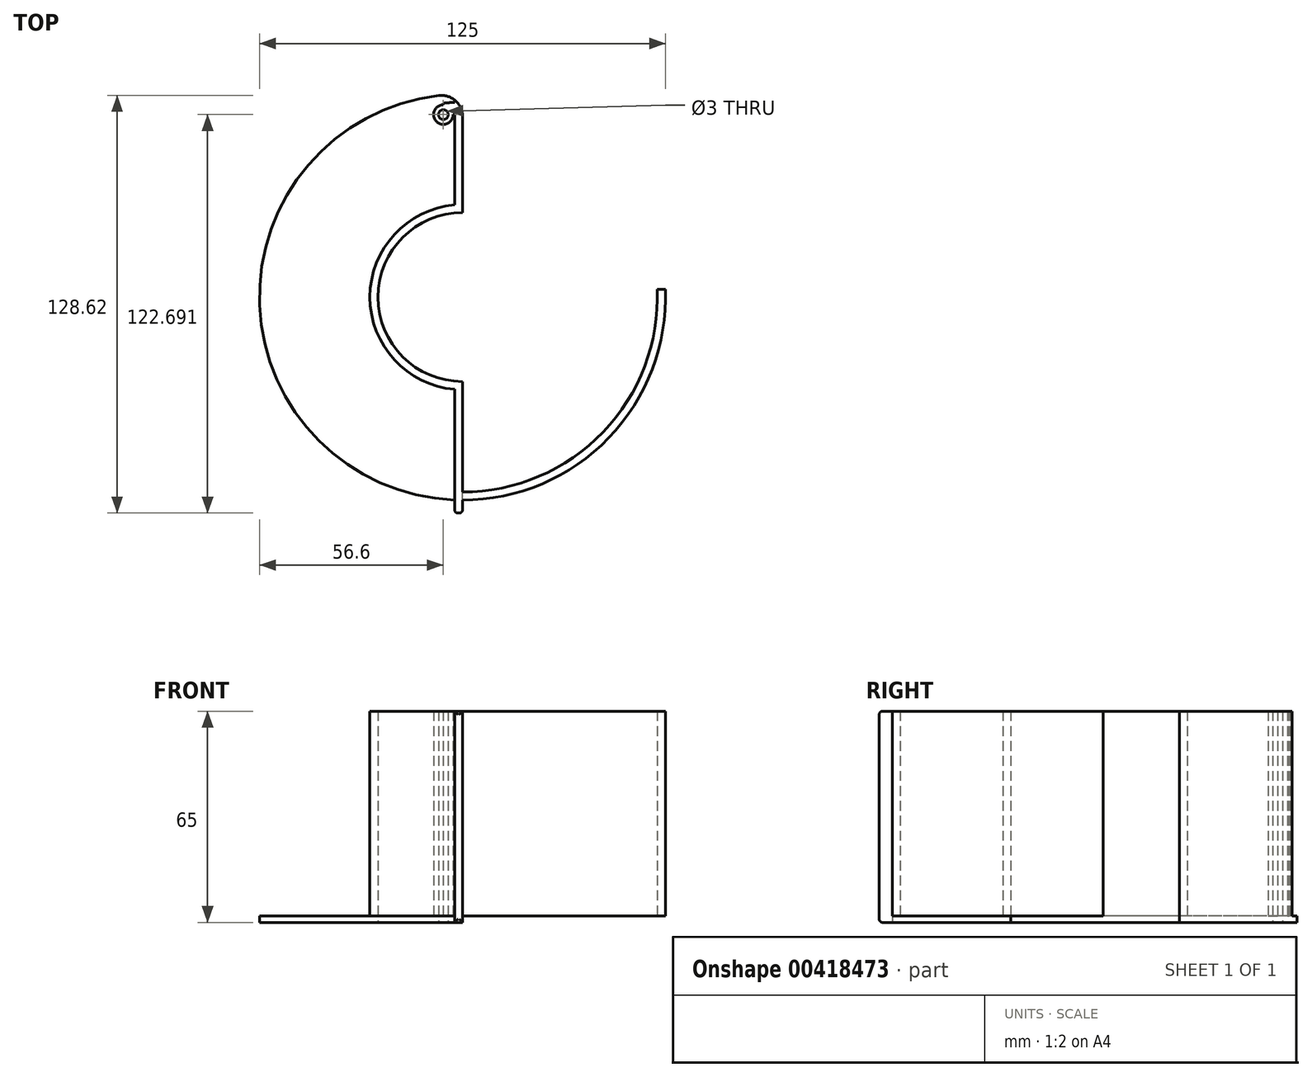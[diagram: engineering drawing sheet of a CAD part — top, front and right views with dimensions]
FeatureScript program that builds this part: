
annotation { "Feature Type Name" : "Feature", "Feature Type Description" : "" }
export const myFeature = defineFeature(function(context is Context, id is Id, definition is map)
    precondition{}
    {
        {
            var Q0;
            Q0=qCreatedBy(makeId("Top.planeOp"),FACE);
            var sketch = newSketch(context, id + "F0", { "sketchPlane" : qUnion([Q0])});
            skCircle(sketch, "E0", {"center": v(0, 0) * mm, "radius": 62.5 * mm});
            skCircle(sketch, "E1", {"center": v(0, 0) * mm, "radius": 26 * mm});
            skCircle(sketch, "E2", {"center": v(0, 0) * mm, "radius": 60 * mm});
            skCircle(sketch, "E3", {"center": v(0, 0) * mm, "radius": 28.5 * mm});
            skLineSegment(sketch, "E4", {"start": v(0, 62.5) * mm, "end": v(0, -62.5) * mm});
            skLineSegment(sketch, "E5", {"start": v(-62.5, 0) * mm, "end": v(62.5, 0) * mm});
            skLineSegment(sketch, "E6", {"start": v(-62.45, 2.4) * mm, "end": v(62.45, 2.4) * mm});
            skLineSegment(sketch, "E7", {"start": v(-2.4, 62.45) * mm, "end": v(-2.4, -62.45) * mm});
            skPoint(sketch, "E8", {"position": v(-5.9, 56.2) * mm});
            skCircle(sketch, "E9", {"center": v(-5.9, 56.2) * mm, "radius": 3 * mm});
            skCircle(sketch, "E10", {"center": v(-5.9, 56.2) * mm, "radius": 1.5 * mm});
            skLineSegment(sketch, "E11", {"start": v(-5.9, 56.2) * mm, "end": v(-5.9, 59.7) * mm});
            skLineSegment(sketch, "E12", {"start": v(-5.9, 56.2) * mm, "end": v(-2.4, 56.2) * mm});
            skPoint(sketch, "E13.orphan", {"position": v(-2.4, 0) * mm});
            skSolve(sketch);
        }
        {
            var Q0;
            Q0=qCreatedBy(makeId("Top.planeOp"),FACE);
            var sketch = newSketch(context, id + "F1", { "sketchPlane" : qUnion([Q0])});
            skCircle(sketch, "E14", {"center": v(0, 0) * mm, "radius": 62.5 * mm});
            skLineSegment(sketch, "E15", {"start": v(0, -62.5) * mm, "end": v(0, 62.5) * mm});
            skLineSegment(sketch, "E16", {"start": v(-62.5, 0) * mm, "end": v(62.5, 0) * mm});
            skCircle(sketch, "E17", {"center": v(0, 0) * mm, "radius": 26 * mm});
            skSolve(sketch);
        }
        {
            var Q0;
            {var subQ0=sQuery(id+"F0.wireOp",EDGE,"E6");var subQ1=sQuery(id+"F0.wireOp",EDGE,"E0");var subQ2=makeQuery(id+"F0.imprint","INTERSECT",VERTEX,{"disambiguationData":[OD(0.0)],"derivedFrom":[subQ1,subQ0]});Q0=makeQuery(id+"F0.imprint","IMPRINT",FACE,{"disambiguationData":[TD([[makeQuery(id+"F0.imprint","IMPRINT",EDGE,{"disambiguationData":[TD([[subQ2,1.0]])],"derivedFrom":subQ1}),1.0]])]});}
            var Q1;
            {var subQ0=sQuery(id+"F0.wireOp",EDGE,"E4");var subQ1=sQuery(id+"F0.wireOp",EDGE,"E0");var subQ2=makeQuery(id+"F0.imprint","INTERSECT",VERTEX,{"disambiguationData":[OD(0.0)],"derivedFrom":[subQ1,subQ0]});Q1=makeQuery(id+"F0.imprint","IMPRINT",FACE,{"disambiguationData":[TD([[makeQuery(id+"F0.imprint","IMPRINT",EDGE,{"disambiguationData":[TD([[subQ2,-1.0]])],"derivedFrom":subQ1}),1.0]])]});}
            var Q2;
            {var subQ0=sQuery(id+"F0.wireOp",EDGE,"E4");var subQ1=sQuery(id+"F0.wireOp",EDGE,"E2");var subQ2=makeQuery(id+"F0.imprint","INTERSECT",VERTEX,{"disambiguationData":[OD(0.0)],"derivedFrom":[subQ1,subQ0]});Q2=makeQuery(id+"F0.imprint","IMPRINT",FACE,{"disambiguationData":[TD([[makeQuery(id+"F0.imprint","IMPRINT",EDGE,{"disambiguationData":[TD([[subQ2,-1.0]])],"derivedFrom":subQ1}),1.0]])]});}
            var Q3;
            {var subQ0=sQuery(id+"F0.wireOp",EDGE,"E4");var subQ1=sQuery(id+"F0.wireOp",EDGE,"E1");var subQ2=makeQuery(id+"F0.imprint","INTERSECT",VERTEX,{"disambiguationData":[OD(0.0)],"derivedFrom":[subQ1,subQ0]});Q3=makeQuery(id+"F0.imprint","IMPRINT",FACE,{"disambiguationData":[TD([[makeQuery(id+"F0.imprint","IMPRINT",EDGE,{"disambiguationData":[TD([[subQ2,-1.0]])],"derivedFrom":subQ1}),-1.0]])]});}
            var Q4;
            {var subQ0=sQuery(id+"F0.wireOp",EDGE,"E7");var subQ1=sQuery(id+"F0.wireOp",EDGE,"E1");var subQ2=makeQuery(id+"F0.imprint","INTERSECT",VERTEX,{"derivedFrom":[subQ1,subQ0]});Q4=makeQuery(id+"F0.imprint","IMPRINT",FACE,{"disambiguationData":[TD([[makeQuery(id+"F0.imprint","IMPRINT",EDGE,{"disambiguationData":[TD([[subQ2,-1.0]])],"derivedFrom":subQ1}),-1.0]])]});}
            var Q5;
            {var subQ0=sQuery(id+"F0.wireOp",EDGE,"E6");var subQ1=sQuery(id+"F0.wireOp",EDGE,"E1");var subQ2=makeQuery(id+"F0.imprint","INTERSECT",VERTEX,{"disambiguationData":[OD(1.0)],"derivedFrom":[subQ1,subQ0]});Q5=makeQuery(id+"F0.imprint","IMPRINT",FACE,{"disambiguationData":[TD([[makeQuery(id+"F0.imprint","IMPRINT",EDGE,{"disambiguationData":[TD([[subQ2,-1.0]])],"derivedFrom":subQ1}),-1.0]])]});}
            var Q6;
            {var subQ0=sQuery(id+"F0.wireOp",EDGE,"E5");var subQ1=sQuery(id+"F0.wireOp",EDGE,"E0");var subQ2=makeQuery(id+"F0.imprint","INTERSECT",VERTEX,{"disambiguationData":[OD(0.0)],"derivedFrom":[subQ1,subQ0]});Q6=makeQuery(id+"F0.imprint","IMPRINT",FACE,{"disambiguationData":[TD([[makeQuery(id+"F0.imprint","IMPRINT",EDGE,{"disambiguationData":[TD([[subQ2,1.0]])],"derivedFrom":subQ1}),1.0]])]});}
            var Q7;
            Q7=makeQuery(id+"F0.imprint","IMPRINT",FACE,{"disambiguationData":[TD([[makeQuery(id+"F0.imprint","IMPRINT",EDGE,{"derivedFrom":sQuery(id+"F0.wireOp",EDGE,"E9")}),1.0]])]});
            var Q8;
            {var subQ0=sQuery(id+"F0.wireOp",EDGE,"E11");var subQ1=sQuery(id+"F0.wireOp",EDGE,"E2");var subQ2=makeQuery(id+"F0.imprint","INTERSECT",VERTEX,{"derivedFrom":[subQ1,subQ0]});Q8=makeQuery(id+"F0.imprint","IMPRINT",FACE,{"disambiguationData":[TD([[makeQuery(id+"F0.imprint","IMPRINT",EDGE,{"disambiguationData":[TD([[subQ2,1.0]])],"derivedFrom":subQ1}),1.0]])]});}
            var Q9;
            {var subQ0=sQuery(id+"F0.wireOp",EDGE,"E5");var subQ1=sQuery(id+"F0.wireOp",EDGE,"E0");var subQ2=makeQuery(id+"F0.imprint","INTERSECT",VERTEX,{"disambiguationData":[OD(0.0)],"derivedFrom":[subQ1,subQ0]});Q9=makeQuery(id+"F0.imprint","IMPRINT",FACE,{"disambiguationData":[TD([[makeQuery(id+"F0.imprint","IMPRINT",EDGE,{"disambiguationData":[TD([[subQ2,-1.0]])],"derivedFrom":subQ1}),1.0]])]});}
            var Q10;
            {var subQ0=sQuery(id+"F0.wireOp",EDGE,"E5");var subQ1=sQuery(id+"F0.wireOp",EDGE,"E1");var subQ2=makeQuery(id+"F0.imprint","INTERSECT",VERTEX,{"disambiguationData":[OD(1.0)],"derivedFrom":[subQ1,subQ0]});Q10=makeQuery(id+"F0.imprint","IMPRINT",FACE,{"disambiguationData":[TD([[makeQuery(id+"F0.imprint","IMPRINT",EDGE,{"disambiguationData":[TD([[subQ2,-1.0]])],"derivedFrom":subQ1}),-1.0]])]});}
            var Q11;
            {var subQ0=sQuery(id+"F0.wireOp",EDGE,"E7");var subQ1=sQuery(id+"F0.wireOp",EDGE,"E2");var subQ2=makeQuery(id+"F0.imprint","INTERSECT",VERTEX,{"disambiguationData":[OD(1.0)],"derivedFrom":[subQ1,subQ0]});Q11=makeQuery(id+"F0.imprint","IMPRINT",FACE,{"disambiguationData":[TD([[makeQuery(id+"F0.imprint","IMPRINT",EDGE,{"disambiguationData":[TD([[subQ2,-1.0]])],"derivedFrom":subQ1}),1.0]])]});}
            var Q12;
            {var subQ0=sQuery(id+"F0.wireOp",EDGE,"E4");var subQ1=sQuery(id+"F0.wireOp",EDGE,"E0");var subQ2=makeQuery(id+"F0.imprint","INTERSECT",VERTEX,{"disambiguationData":[OD(1.0)],"derivedFrom":[subQ1,subQ0]});Q12=makeQuery(id+"F0.imprint","IMPRINT",FACE,{"disambiguationData":[TD([[makeQuery(id+"F0.imprint","IMPRINT",EDGE,{"disambiguationData":[TD([[subQ2,1.0]])],"derivedFrom":subQ1}),1.0]])]});}
            extrude(context, id + "F2", {"entities" : qUnion([Q0, Q1, Q2, Q3, Q4, Q5, Q6, Q7, Q8, Q9, Q10, Q11, Q12]), "depth" : 63 * mm});
        }
        {
            var Q0;
            {var subQ0=sQuery(id+"F1.wireOp",EDGE,"E15");var subQ1=sQuery(id+"F1.wireOp",EDGE,"E14");var subQ2=makeQuery(id+"F1.imprint","INTERSECT",VERTEX,{"disambiguationData":[OD(1.0)],"derivedFrom":[subQ1,subQ0]});Q0=makeQuery(id+"F1.imprint","IMPRINT",FACE,{"disambiguationData":[TD([[makeQuery(id+"F1.imprint","IMPRINT",EDGE,{"disambiguationData":[TD([[subQ2,-1.0]])],"derivedFrom":subQ1}),1.0]])]});}
            var Q1;
            {var subQ0=sQuery(id+"F1.wireOp",EDGE,"E15");var subQ1=sQuery(id+"F1.wireOp",EDGE,"E14");var subQ2=makeQuery(id+"F1.imprint","INTERSECT",VERTEX,{"disambiguationData":[OD(0.0)],"derivedFrom":[subQ1,subQ0]});Q1=makeQuery(id+"F1.imprint","IMPRINT",FACE,{"disambiguationData":[TD([[makeQuery(id+"F1.imprint","IMPRINT",EDGE,{"disambiguationData":[TD([[subQ2,1.0]])],"derivedFrom":subQ1}),1.0]])]});}
            extrude(context, id + "F3", {"entities" : qUnion([Q0, Q1]), "operationType" : NewBodyOperationType.ADD, "oppositeDirection" : true, "depth" : 2 * mm});
        }
        {
            var Q0;
            {var subQ0=sQuery(id+"F1.wireOp",EDGE,"E15");var subQ1=sQuery(id+"F0.wireOp",EDGE,"E4");var subQ2=makeQuery(id+"F0.imprint","INTERSECT",VERTEX,{"disambiguationData":[OD(1.0)],"derivedFrom":[sQuery(id+"F0.wireOp",EDGE,"E2"),subQ1]});Q0=makeQuery(id+"F3.boolean.opBoolean","MERGE",FACE,{"derivedFrom":[makeQuery(id+"F2.opExtrude","SWEPT_FACE",FACE,{"disambiguationData":[OSD([subQ1]),TDD([makeQuery(id+"F0.imprint","IMPRINT",EDGE,{"disambiguationData":[TD([[makeQuery(id+"F0.imprint","INTERSECT",VERTEX,{"disambiguationData":[OD(1.0)],"derivedFrom":[sQuery(id+"F0.wireOp",EDGE,"E1"),subQ1]}),-1.0]])],"derivedFrom":subQ1}),makeQuery(id+"F0.imprint","IMPRINT",EDGE,{"disambiguationData":[TD([[subQ2,1.0]])],"derivedFrom":subQ1}),makeQuery(id+"F0.imprint","IMPRINT",EDGE,{"disambiguationData":[TD([[makeQuery(id+"F0.imprint","INTERSECT",VERTEX,{"disambiguationData":[OD(1.0)],"derivedFrom":[sQuery(id+"F0.wireOp",EDGE,"E0"),subQ1]}),1.0]])],"derivedFrom":subQ1})])]}),makeQuery(id+"F3.opExtrude","SWEPT_FACE",FACE,{"disambiguationData":[OSD([subQ0]),TDD([makeQuery(id+"F1.imprint","IMPRINT",EDGE,{"disambiguationData":[TD([[makeQuery(id+"F1.imprint","INTERSECT",VERTEX,{"disambiguationData":[OD(0.0)],"derivedFrom":[sQuery(id+"F1.wireOp",EDGE,"E14"),subQ0]}),-1.0]])],"derivedFrom":subQ0})])]})]});}
            var sketch = newSketch(context, id + "F4", { "sketchPlane" : qUnion([Q0])});
            skLineSegment(sketch, "E18.bottom", {"start": v(-26, 63) * mm, "end": v(-66.5, 63) * mm});
            skLineSegment(sketch, "E18.top", {"start": v(-26, -2) * mm, "end": v(-66.5, -2) * mm});
            skLineSegment(sketch, "E18.left", {"start": v(-26, 63) * mm, "end": v(-26, -2) * mm});
            skLineSegment(sketch, "E18.right", {"start": v(-66.5, 63) * mm, "end": v(-66.5, -2) * mm});
            skSolve(sketch);
        }
        {
            var Q0;
            {var subQ6=sQuery(id+"F4.wireOp",EDGE,"E18.left");Q0=makeQuery(id+"F4.imprint","IMPRINT",FACE,{"disambiguationData":[TD([[makeQuery(id+"F4.imprint","IMPRINT",EDGE,{"derivedFrom":subQ6}),-1.0]])]});}
            var Q1;
            {var subQ6=sQuery(id+"F4.wireOp",EDGE,"E18.right");Q1=makeQuery(id+"F4.imprint","IMPRINT",FACE,{"disambiguationData":[TD([[makeQuery(id+"F4.imprint","IMPRINT",EDGE,{"derivedFrom":subQ6}),1.0]])]});}
            extrude(context, id + "F5", {"entities" : qUnion([Q0, Q1]), "operationType" : NewBodyOperationType.ADD, "oppositeDirection" : true, "depth" : 2.4 * mm});
        }
        {
            var Q0;
            Q0=makeQuery(id+"F5.opExtrude","CAP_EDGE",EDGE,{"disambiguationData":[OSD([sQuery(id+"F4.wireOp",EDGE,"E18.right")])],"isStart":true});
            var Q1;
            Q1=makeQuery(id+"F5.opExtrude","SWEPT_EDGE",EDGE,{"disambiguationData":[OSD([sQuery(id+"F4.wireOp",EDGE,"E18.bottom"),sQuery(id+"F4.wireOp",EDGE,"E18.right")])]});
            var Q2;
            Q2=makeQuery(id+"F5.opExtrude","CAP_EDGE",EDGE,{"disambiguationData":[OSD([sQuery(id+"F4.wireOp",EDGE,"E18.right")])],"isStart":false});
            var Q3;
            Q3=makeQuery(id+"F5.opExtrude","SWEPT_EDGE",EDGE,{"disambiguationData":[OSD([sQuery(id+"F4.wireOp",EDGE,"E18.top"),sQuery(id+"F4.wireOp",EDGE,"E18.right")])]});
            fillet(context, id + "F6", {"entities" : qUnion([Q0, Q1, Q2, Q3]), "radius" : 1 * mm, "tangentPropagation" : true, "allowEdgeOverflow" : false});
        }
        {
            var Q0;
            Q0=makeQuery(id+"F5.boolean.opBoolean","MERGE",FACE,{"derivedFrom":[makeQuery(id+"F2.opExtrude","CAP_FACE",FACE,{"disambiguationData":[OSD([sQuery(id+"F0.wireOp",EDGE,"E0"),sQuery(id+"F0.wireOp",EDGE,"E1"),sQuery(id+"F0.wireOp",EDGE,"E2"),sQuery(id+"F0.wireOp",EDGE,"E3"),sQuery(id+"F0.wireOp",EDGE,"E4"),sQuery(id+"F0.wireOp",EDGE,"E7"),sQuery(id+"F0.wireOp",EDGE,"E9"),sQuery(id+"F0.wireOp",EDGE,"E10"),sQuery(id+"F0.wireOp",EDGE,"E11"),sQuery(id+"F0.wireOp",EDGE,"E12")])],"isStart":false}),makeQuery(id+"F5.opExtrude","SWEPT_FACE",FACE,{"disambiguationData":[OSD([sQuery(id+"F4.wireOp",EDGE,"E18.bottom")])]})]});
            var sketch = newSketch(context, id + "F7", { "sketchPlane" : qUnion([Q0])});
            skCircle(sketch, "E19", {"center": v(-5.9, 56.2) * mm, "radius": 1.5 * mm});
            skSolve(sketch);
        }
        {
            var Q0;
            Q0 = qSketchRegion(id + "F7", true);
            extrude(context, id + "F8", {"entities" : qUnion([Q0]), "operationType" : NewBodyOperationType.REMOVE, "endBound" : BoundingType.THROUGH_ALL, "oppositeDirection" : true, "depth" : 25 * mm});
        }
        {
            var Q0;
            {var subQ0=sQuery(id+"F1.wireOp",EDGE,"E15");var subQ1=sQuery(id+"F1.wireOp",EDGE,"E14");var subQ2=sQuery(id+"F0.wireOp",EDGE,"E4");var subQ3=sQuery(id+"F0.wireOp",EDGE,"E0");Q0=makeQuery(id+"F3.boolean.opBoolean","MERGE",EDGE,{"derivedFrom":[makeQuery(id+"F2.opExtrude","SWEPT_EDGE",EDGE,{"disambiguationData":[OSD([subQ3,subQ2]),TDD([makeQuery(id+"F0.imprint","INTERSECT",VERTEX,{"disambiguationData":[OD(0.0)],"derivedFrom":[subQ3,subQ2]})])]}),makeQuery(id+"F3.opExtrude","SWEPT_EDGE",EDGE,{"disambiguationData":[OSD([subQ1,subQ0]),TDD([makeQuery(id+"F1.imprint","INTERSECT",VERTEX,{"disambiguationData":[OD(1.0)],"derivedFrom":[subQ1,subQ0]})])]})]});}
            fillet(context, id + "F9", {"entities" : qUnion([Q0]), "radius" : 6.5 * mm, "tangentPropagation" : true, "allowEdgeOverflow" : false});
        }
    });
